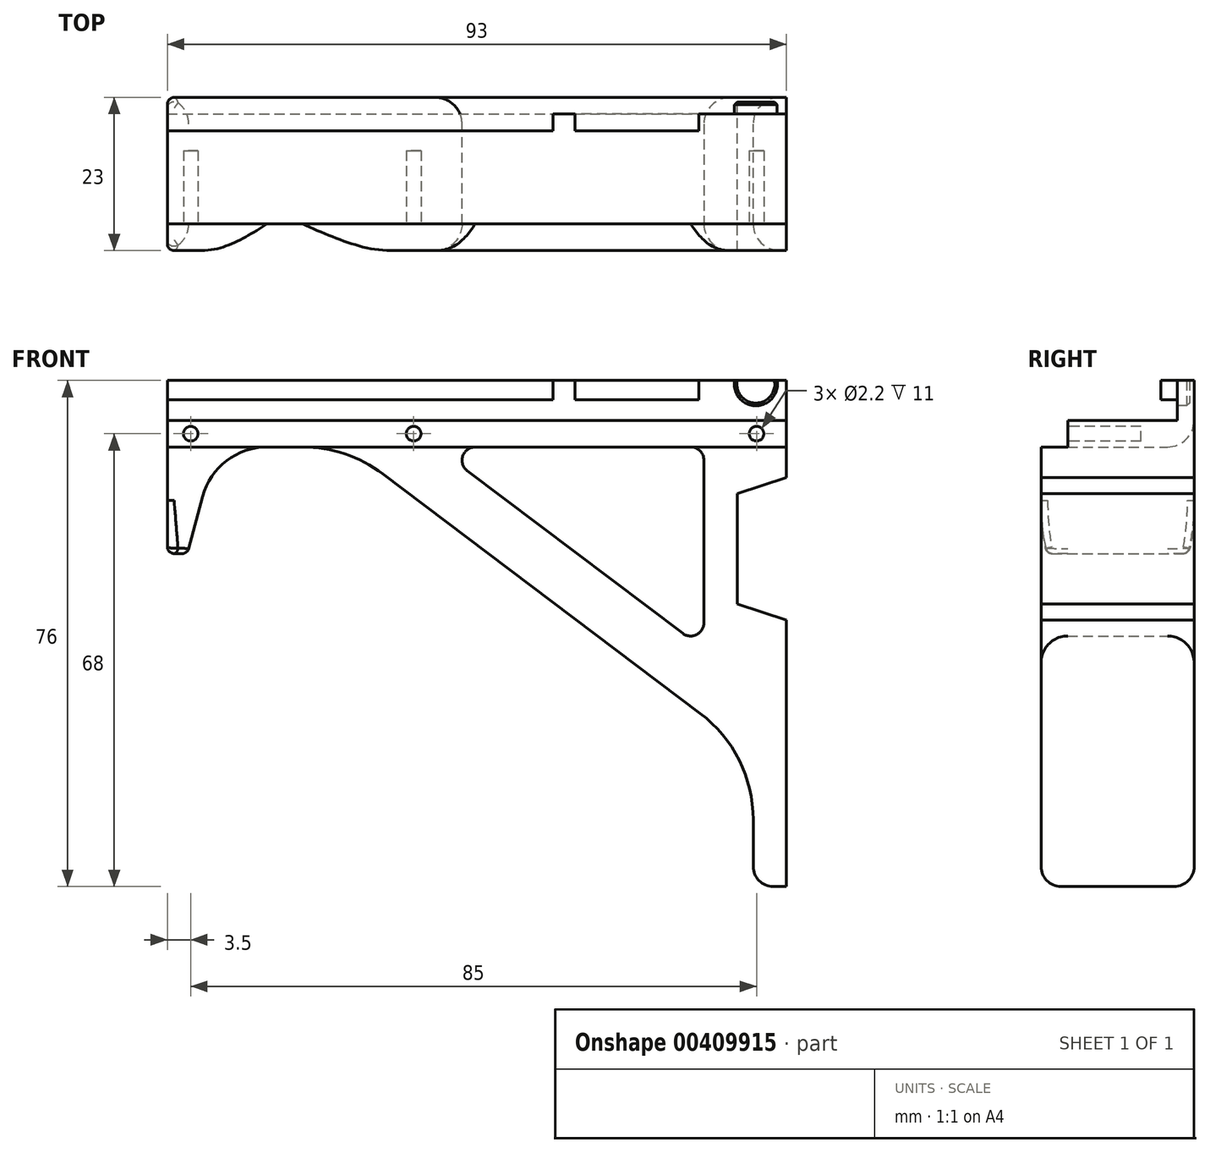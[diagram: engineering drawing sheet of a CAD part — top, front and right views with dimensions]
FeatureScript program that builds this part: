
annotation { "Feature Type Name" : "Feature", "Feature Type Description" : "" }
export const myFeature = defineFeature(function(context is Context, id is Id, definition is map)
    precondition{}
    {
        {
            var Q0;
            Q0=qCreatedBy(makeId("Front.planeOp"),FACE);
            var sketch = newSketch(context, id + "F0", { "sketchPlane" : qUnion([Q0])});
            skLineSegment(sketch, "E0", {"start": v(0, 0) * mm, "end": v(-93, 0) * mm});
            skLineSegment(sketch, "E1", {"start": v(0, 0) * mm, "end": v(0, -8.6) * mm});
            skLineSegment(sketch, "E2.0", {"start": v(0, -8.6) * mm, "end": v(-93, -8.6) * mm, "construction": true});
            skLineSegment(sketch, "E3.0", {"start": v(-7.4, 0) * mm, "end": v(-7.4, -30) * mm, "construction": true});
            skLineSegment(sketch, "E4.0", {"start": v(0, -30) * mm, "end": v(-93, -30) * mm, "construction": true});
            skLineSegment(sketch, "E5.0", {"start": v(0, -11) * mm, "end": v(-93, -11) * mm, "construction": true});
            skLineSegment(sketch, "E6.0", {"start": v(0, -27.6) * mm, "end": v(-93, -27.6) * mm, "construction": true});
            skLineSegment(sketch, "E7", {"start": v(0, -8.6) * mm, "end": v(-7.4, -11) * mm});
            skLineSegment(sketch, "E8", {"start": v(-7.4, -11) * mm, "end": v(-7.4, -27.6) * mm});
            skLineSegment(sketch, "E9", {"start": v(-7.4, -27.6) * mm, "end": v(0, -30) * mm});
            skLineSegment(sketch, "E10.trimOffspring", {"start": v(0, -30) * mm, "end": v(0, -70) * mm});
            skLineSegment(sketch, "E11.0", {"start": v(-5, -59.97) * mm, "end": v(-5, -70) * mm});
            skLineSegment(sketch, "E12", {"start": v(0, -70) * mm, "end": v(-5, -70) * mm});
            skLineSegment(sketch, "E13.0", {"start": v(-72.7, -4) * mm, "end": v(-78.04, -4) * mm});
            skLineSegment(sketch, "E14.0", {"start": v(-90, -20) * mm, "end": v(-93, -20) * mm});
            skLineSegment(sketch, "E15", {"start": v(-93, 0) * mm, "end": v(-93, -20) * mm});
            skLineSegment(sketch, "E16.0", {"start": v(-90, -11) * mm, "end": v(-90, -20) * mm, "construction": true});
            skLineSegment(sketch, "E17", {"start": v(-90, -20) * mm, "end": v(-87.7, -11.41) * mm});
            skLineSegment(sketch, "E18.0", {"start": v(-66, -5) * mm, "end": v(-66, -20) * mm, "construction": true});
            skLineSegment(sketch, "E19.0", {"start": v(0, -50) * mm, "end": v(-5, -50) * mm, "construction": true});
            skLineSegment(sketch, "E20", {"start": v(-60.65, -8.03) * mm, "end": v(-12.96, -44) * mm});
            skPoint(sketch, "E21.visualSharp", {"position": v(-85.71, -4) * mm});
            skArc(sketch, "E21.filletArc", {"start": v(-78.04, -4) * mm, "mid": v(-84.13, -6.07) * mm, "end": v(-87.7, -11.41) * mm});
            skPoint(sketch, "E22.visualSharp", {"position": v(-66, -4) * mm});
            skArc(sketch, "E22.filletArc", {"start": v(-60.65, -8.03) * mm, "mid": v(-66.35, -5.03) * mm, "end": v(-72.7, -4) * mm});
            skPoint(sketch, "E23.visualSharp", {"position": v(-5, -50) * mm});
            skArc(sketch, "E23.filletArc", {"start": v(-5, -59.97) * mm, "mid": v(-7.1, -51.05) * mm, "end": v(-12.96, -44) * mm});
            skSolve(sketch);
        }
        {
            var Q0;
            Q0 = qSketchRegion(id + "F0", true);
            extrude(context, id + "F1", {"entities" : qUnion([Q0]), "depth" : 23 * mm});
        }
        {
            var Q0;
            Q0=makeQuery(id+"F1.opExtrude","SWEPT_FACE",FACE,{"disambiguationData":[OSD([sQuery(id+"F0.wireOp",EDGE,"E20")])]});
            var Q1;
            Q1=makeQuery(id+"F1.opExtrude","SWEPT_FACE",FACE,{"disambiguationData":[OSD([sQuery(id+"F0.wireOp",EDGE,"E13.0")])]});
            fillet(context, id + "F2", {"entities" : qUnion([Q0, Q1]), "radius" : 4 * mm, "tangentPropagation" : true, "allowEdgeOverflow" : false});
        }
        {
            var Q0;
            Q0=makeQuery(id+"F1.opExtrude","SWEPT_FACE",FACE,{"disambiguationData":[OSD([sQuery(id+"F0.wireOp",EDGE,"E0")])]});
            var sketch = newSketch(context, id + "F3", { "sketchPlane" : qUnion([Q0])});
            skLineSegment(sketch, "E24", {"start": v(-93, 0) * mm, "end": v(0, 0) * mm});
            skLineSegment(sketch, "E25.0", {"start": v(-93, -2.5) * mm, "end": v(0, -2.5) * mm});
            skLineSegment(sketch, "E26", {"start": v(-93, 0) * mm, "end": v(-93, -2.5) * mm});
            skLineSegment(sketch, "E27", {"start": v(0, 0) * mm, "end": v(0, -2.5) * mm});
            skLineSegment(sketch, "E28", {"start": v(-93, -23) * mm, "end": v(0, -23) * mm});
            skLineSegment(sketch, "E29", {"start": v(0, -23) * mm, "end": v(0, -20.5) * mm});
            skLineSegment(sketch, "E30", {"start": v(0, -20.5) * mm, "end": v(-93, -20.5) * mm});
            skLineSegment(sketch, "E31", {"start": v(-93, -20.5) * mm, "end": v(-93, -23) * mm});
            skSolve(sketch);
        }
        {
            var Q0;
            Q0 = qSketchRegion(id + "F3", true);
            extrude(context, id + "F4", {"entities" : qUnion([Q0]), "operationType" : NewBodyOperationType.ADD, "depth" : 6 * mm});
        }
        {
            var Q0;
            Q0=makeQuery(id+"F4.opExtrude","SWEPT_FACE",FACE,{"disambiguationData":[OSD([sQuery(id+"F3.wireOp",EDGE,"E25.0")])]});
            var sketch = newSketch(context, id + "F5", { "sketchPlane" : qUnion([Q0])});
            skLineSegment(sketch, "E32", {"start": v(-93, 6) * mm, "end": v(-35.1, 6) * mm});
            skLineSegment(sketch, "E33", {"start": v(0, 6) * mm, "end": v(0, 3.1) * mm, "construction": true});
            skLineSegment(sketch, "E34", {"start": v(-13.2, 3.1) * mm, "end": v(-31.8, 3.1) * mm});
            skLineSegment(sketch, "E35", {"start": v(-93, 3.1) * mm, "end": v(-93, 6) * mm});
            skLineSegment(sketch, "E36.0", {"start": v(-13.2, 6) * mm, "end": v(-13.2, 3.1) * mm});
            skLineSegment(sketch, "E37.0", {"start": v(-31.8, 6) * mm, "end": v(-31.8, 3.1) * mm});
            skLineSegment(sketch, "E38.0", {"start": v(-35.1, 6) * mm, "end": v(-35.1, 3.1) * mm});
            skLineSegment(sketch, "E39.trimOffspring", {"start": v(-31.8, 6) * mm, "end": v(-13.2, 6) * mm});
            skLineSegment(sketch, "E40.trimOffspring", {"start": v(-35.1, 3.1) * mm, "end": v(-93, 3.1) * mm});
            skSolve(sketch);
        }
        {
            var Q0;
            Q0 = qSketchRegion(id + "F5", true);
            extrude(context, id + "F6", {"entities" : qUnion([Q0]), "operationType" : NewBodyOperationType.ADD, "depth" : 2.5 * mm});
        }
        {
            var Q0;
            Q0=makeQuery(id+"F4.opExtrude","SWEPT_FACE",FACE,{"disambiguationData":[OSD([sQuery(id+"F3.wireOp",EDGE,"E30")])]});
            var sketch = newSketch(context, id + "F7", { "sketchPlane" : qUnion([Q0])});
            skLineSegment(sketch, "E41", {"start": v(13.2, 6) * mm, "end": v(31.8, 6) * mm});
            skLineSegment(sketch, "E42", {"start": v(93, 6) * mm, "end": v(93, 3.1) * mm});
            skLineSegment(sketch, "E43", {"start": v(93, 3.1) * mm, "end": v(35.1, 3.1) * mm});
            skLineSegment(sketch, "E44", {"start": v(0, 3.1) * mm, "end": v(0, 6) * mm, "construction": true});
            skLineSegment(sketch, "E45.0", {"start": v(13.2, 3.1) * mm, "end": v(13.2, 6) * mm});
            skLineSegment(sketch, "E46.0", {"start": v(31.8, 3.1) * mm, "end": v(31.8, 6) * mm});
            skLineSegment(sketch, "E47.0", {"start": v(35.1, 3.1) * mm, "end": v(35.1, 6) * mm});
            skLineSegment(sketch, "E48.trimOffspring", {"start": v(35.1, 6) * mm, "end": v(93, 6) * mm});
            skLineSegment(sketch, "E49.trimOffspring", {"start": v(31.8, 3.1) * mm, "end": v(13.2, 3.1) * mm});
            skSolve(sketch);
        }
        {
            var Q0;
            Q0 = qSketchRegion(id + "F7", true);
            extrude(context, id + "F8", {"entities" : qUnion([Q0]), "operationType" : NewBodyOperationType.ADD, "depth" : 2.5 * mm});
        }
        {
            var Q0;
            {var subQ0=makeQuery(id+"F1.opExtrude","CAP_FACE",FACE,{"disambiguationData":[OSD([sQuery(id+"F0.wireOp",EDGE,"E0"),sQuery(id+"F0.wireOp",EDGE,"E1"),sQuery(id+"F0.wireOp",EDGE,"E7"),sQuery(id+"F0.wireOp",EDGE,"E8"),sQuery(id+"F0.wireOp",EDGE,"E9"),sQuery(id+"F0.wireOp",EDGE,"E10.trimOffspring"),sQuery(id+"F0.wireOp",EDGE,"E11.0"),sQuery(id+"F0.wireOp",EDGE,"E12"),sQuery(id+"F0.wireOp",EDGE,"E13.0"),sQuery(id+"F0.wireOp",EDGE,"E14.0"),sQuery(id+"F0.wireOp",EDGE,"E15"),sQuery(id+"F0.wireOp",EDGE,"E17"),sQuery(id+"F0.wireOp",EDGE,"E20")])],"isStart":false});Q0=makeQuery(id+"F4.boolean.opBoolean","MERGE",FACE,{"derivedFrom":[makeQuery(id+"F2.opFillet","SPLIT",FACE,{"disambiguationData":[OD(0.0)],"derivedFrom":subQ0}),makeQuery(id+"F2.opFillet","SPLIT",FACE,{"disambiguationData":[OD(1.0)],"derivedFrom":subQ0}),makeQuery(id+"F4.opExtrude","SWEPT_FACE",FACE,{"disambiguationData":[OSD([sQuery(id+"F3.wireOp",EDGE,"E28")])]})]});}
            var sketch = newSketch(context, id + "F9", { "sketchPlane" : qUnion([Q0])});
            skLineSegment(sketch, "E50", {"start": v(-52.71, -4) * mm, "end": v(-12.4, -4) * mm});
            skLineSegment(sketch, "E51", {"start": v(-12.4, -4) * mm, "end": v(-12.4, -34.4) * mm});
            skLineSegment(sketch, "E52", {"start": v(-12.4, -34.4) * mm, "end": v(-52.71, -4) * mm});
            skSolve(sketch);
        }
        {
            var Q0;
            Q0 = qSketchRegion(id + "F9", true);
            extrude(context, id + "F10", {"entities" : qUnion([Q0]), "operationType" : NewBodyOperationType.REMOVE, "endBound" : BoundingType.THROUGH_ALL, "oppositeDirection" : true, "depth" : 25 * mm});
        }
        {
            var Q0;
            Q0=makeQuery(id+"F10.boolean.opBoolean","COPY",EDGE,{"derivedFrom":makeQuery(id+"F10.opExtrude","SWEPT_EDGE",EDGE,{"disambiguationData":[OSD([sQuery(id+"F9.wireOp",EDGE,"E50"),sQuery(id+"F9.wireOp",EDGE,"E52")])]})});
            var Q1;
            Q1=makeQuery(id+"F10.boolean.opBoolean","COPY",EDGE,{"derivedFrom":makeQuery(id+"F10.opExtrude","SWEPT_EDGE",EDGE,{"disambiguationData":[OSD([sQuery(id+"F9.wireOp",EDGE,"E50"),sQuery(id+"F9.wireOp",EDGE,"E51")])]})});
            var Q2;
            Q2=makeQuery(id+"F10.boolean.opBoolean","COPY",EDGE,{"derivedFrom":makeQuery(id+"F10.opExtrude","SWEPT_EDGE",EDGE,{"disambiguationData":[OSD([sQuery(id+"F9.wireOp",EDGE,"E51"),sQuery(id+"F9.wireOp",EDGE,"E52")])]})});
            fillet(context, id + "F11", {"entities" : qUnion([Q0, Q1, Q2]), "radius" : 2 * mm, "tangentPropagation" : true, "allowEdgeOverflow" : false});
        }
        {
            var Q0;
            Q0=makeQuery(id+"F10.boolean.opBoolean","COPY",FACE,{"derivedFrom":makeQuery(id+"F10.opExtrude","SWEPT_FACE",FACE,{"disambiguationData":[OSD([sQuery(id+"F9.wireOp",EDGE,"E52")])]})});
            var Q1;
            Q1=makeQuery(id+"F11.opFillet","BLEND_FACE",FACE,{"disambiguationData":[OSD([sQuery(id+"F9.wireOp",EDGE,"E50"),sQuery(id+"F9.wireOp",EDGE,"E52")])]});
            var Q2;
            Q2=makeQuery(id+"F11.opFillet","BLEND_FACE",FACE,{"disambiguationData":[OSD([sQuery(id+"F9.wireOp",EDGE,"E51"),sQuery(id+"F9.wireOp",EDGE,"E52")])]});
            var Q3;
            Q3=makeQuery(id+"F10.boolean.opBoolean","COPY",FACE,{"derivedFrom":makeQuery(id+"F10.opExtrude","SWEPT_FACE",FACE,{"disambiguationData":[OSD([sQuery(id+"F9.wireOp",EDGE,"E51")])]})});
            var Q4;
            Q4=makeQuery(id+"F11.opFillet","BLEND_FACE",FACE,{"disambiguationData":[OSD([sQuery(id+"F9.wireOp",EDGE,"E50"),sQuery(id+"F9.wireOp",EDGE,"E51")])]});
            var Q5;
            Q5=makeQuery(id+"F10.boolean.opBoolean","COPY",FACE,{"derivedFrom":makeQuery(id+"F10.opExtrude","SWEPT_FACE",FACE,{"disambiguationData":[OSD([sQuery(id+"F9.wireOp",EDGE,"E50")])]})});
            fillet(context, id + "F12", {"entities" : qUnion([Q0, Q1, Q2, Q3, Q4, Q5]), "radius" : 4 * mm, "tangentPropagation" : true, "allowEdgeOverflow" : false});
        }
        {
            var Q0;
            Q0=makeQuery(id+"F1.opExtrude","SWEPT_FACE",FACE,{"disambiguationData":[OSD([sQuery(id+"F0.wireOp",EDGE,"E14.0")])]});
            var Q1;
            Q1=makeQuery(id+"F4.boolean.opBoolean","MERGE",EDGE,{"derivedFrom":[makeQuery(id+"F1.opExtrude","CAP_EDGE",EDGE,{"disambiguationData":[OSD([sQuery(id+"F0.wireOp",EDGE,"E15")])],"isStart":false}),makeQuery(id+"F4.opExtrude","SWEPT_EDGE",EDGE,{"disambiguationData":[OSD([sQuery(id+"F3.wireOp",EDGE,"E28"),sQuery(id+"F3.wireOp",EDGE,"E31")])]})]});
            var Q2;
            Q2=makeQuery(id+"F4.boolean.opBoolean","MERGE",EDGE,{"derivedFrom":[makeQuery(id+"F1.opExtrude","CAP_EDGE",EDGE,{"disambiguationData":[OSD([sQuery(id+"F0.wireOp",EDGE,"E15")])],"isStart":true}),makeQuery(id+"F4.opExtrude","SWEPT_EDGE",EDGE,{"disambiguationData":[OSD([sQuery(id+"F3.wireOp",EDGE,"E24"),sQuery(id+"F3.wireOp",EDGE,"E26")])]})]});
            fillet(context, id + "F13", {"entities" : qUnion([Q0, Q1, Q2]), "radius" : 1 * mm, "tangentPropagation" : true, "allowEdgeOverflow" : false});
        }
        {
            var Q0;
            Q0=makeQuery(id+"F4.opExtrude","SWEPT_FACE",FACE,{"disambiguationData":[OSD([sQuery(id+"F3.wireOp",EDGE,"E25.0")])]});
            var sketch = newSketch(context, id + "F14", { "sketchPlane" : qUnion([Q0])});
            skCircle(sketch, "E53", {"center": v(-4.6, 5.45) * mm, "radius": 3.25 * mm});
            skSolve(sketch);
        }
        {
            var Q0;
            Q0 = qSketchRegion(id + "F14", true);
            extrude(context, id + "F15", {"entities" : qUnion([Q0]), "operationType" : NewBodyOperationType.REMOVE, "oppositeDirection" : true, "depth" : 1.8 * mm});
        }
        {
            var Q0;
            Q0=makeQuery(id+"F15.boolean.opBoolean","COPY",EDGE,{"derivedFrom":makeQuery(id+"F15.opExtrude","CAP_EDGE",EDGE,{"disambiguationData":[OSD([sQuery(id+"F14.wireOp",EDGE,"E53")])],"isStart":false})});
            chamfer(context, id + "F16", {"entities" : qUnion([Q0]), "width" : .4 * mm, "tangentPropagation" : true});
        }
        {
            var Q0;
            Q0=makeQuery(id+"F4.opExtrude","SWEPT_FACE",FACE,{"disambiguationData":[OSD([sQuery(id+"F3.wireOp",EDGE,"E30")])]});
            var sketch = newSketch(context, id + "F17", { "sketchPlane" : qUnion([Q0])});
            skCircle(sketch, "E54", {"center": v(4.6, 5.45) * mm, "radius": 3.25 * mm});
            skSolve(sketch);
        }
        {
            var Q0;
            Q0 = qSketchRegion(id + "F17", true);
            extrude(context, id + "F18", {"entities" : qUnion([Q0]), "operationType" : NewBodyOperationType.REMOVE, "oppositeDirection" : true, "depth" : 1.8 * mm});
        }
        {
            var Q0;
            Q0=makeQuery(id+"F18.boolean.opBoolean","COPY",EDGE,{"derivedFrom":makeQuery(id+"F18.opExtrude","CAP_EDGE",EDGE,{"disambiguationData":[OSD([sQuery(id+"F17.wireOp",EDGE,"E54")])],"isStart":false})});
            chamfer(context, id + "F19", {"entities" : qUnion([Q0]), "width" : .4 * mm, "tangentPropagation" : true});
        }
        {
            var Q0;
            {var subQ0=makeQuery(id+"F1.opExtrude","CAP_FACE",FACE,{"disambiguationData":[OSD([sQuery(id+"F0.wireOp",EDGE,"E0"),sQuery(id+"F0.wireOp",EDGE,"E1"),sQuery(id+"F0.wireOp",EDGE,"E7"),sQuery(id+"F0.wireOp",EDGE,"E8"),sQuery(id+"F0.wireOp",EDGE,"E9"),sQuery(id+"F0.wireOp",EDGE,"E10.trimOffspring"),sQuery(id+"F0.wireOp",EDGE,"E11.0"),sQuery(id+"F0.wireOp",EDGE,"E12"),sQuery(id+"F0.wireOp",EDGE,"E13.0"),sQuery(id+"F0.wireOp",EDGE,"E14.0"),sQuery(id+"F0.wireOp",EDGE,"E15"),sQuery(id+"F0.wireOp",EDGE,"E17"),sQuery(id+"F0.wireOp",EDGE,"E20")])],"isStart":false});Q0=makeQuery(id+"F4.boolean.opBoolean","MERGE",FACE,{"derivedFrom":[makeQuery(id+"F2.opFillet","SPLIT",FACE,{"disambiguationData":[OD(0.0)],"derivedFrom":subQ0}),makeQuery(id+"F2.opFillet","SPLIT",FACE,{"disambiguationData":[OD(1.0)],"derivedFrom":subQ0}),makeQuery(id+"F4.opExtrude","SWEPT_FACE",FACE,{"disambiguationData":[OSD([sQuery(id+"F3.wireOp",EDGE,"E28")])]})]});}
            var sketch = newSketch(context, id + "F20", { "sketchPlane" : qUnion([Q0])});
            skCircle(sketch, "E55", {"center": v(-4.5, -2) * mm, "radius": 1.1 * mm});
            skCircle(sketch, "E56", {"center": v(-56, -2) * mm, "radius": 1.1 * mm});
            skCircle(sketch, "E57", {"center": v(-89.5, -2) * mm, "radius": 1.1 * mm});
            skSolve(sketch);
        }
        {
            var Q0;
            Q0 = qSketchRegion(id + "F20", true);
            extrude(context, id + "F21", {"entities" : qUnion([Q0]), "operationType" : NewBodyOperationType.REMOVE, "oppositeDirection" : true, "depth" : 15 * mm});
        }
        {
            var Q0;
            Q0=makeQuery(id+"F4.boolean.opBoolean","MERGE",FACE,{"derivedFrom":[makeQuery(id+"F1.opExtrude","SWEPT_FACE",FACE,{"disambiguationData":[OSD([sQuery(id+"F0.wireOp",EDGE,"E1")])]}),makeQuery(id+"F4.opExtrude","SWEPT_FACE",FACE,{"disambiguationData":[OSD([sQuery(id+"F3.wireOp",EDGE,"E27")])]}),makeQuery(id+"F4.opExtrude","SWEPT_FACE",FACE,{"disambiguationData":[OSD([sQuery(id+"F3.wireOp",EDGE,"E29")])]})]});
            var sketch = newSketch(context, id + "F22", { "sketchPlane" : qUnion([Q0])});
            skLineSegment(sketch, "E58.bottom", {"start": v(-23, 6) * mm, "end": v(-19, 6) * mm});
            skLineSegment(sketch, "E58.top", {"start": v(-23, -4) * mm, "end": v(-19, -4) * mm});
            skLineSegment(sketch, "E58.left", {"start": v(-23, 6) * mm, "end": v(-23, -4) * mm});
            skLineSegment(sketch, "E58.right", {"start": v(-19, 3.1) * mm, "end": v(-19, -4) * mm});
            skLineSegment(sketch, "E59.bottom", {"start": v(-19, 6) * mm, "end": v(-18, 6) * mm});
            skLineSegment(sketch, "E59.top", {"start": v(-19, 3.1) * mm, "end": v(-18, 3.1) * mm});
            skLineSegment(sketch, "E59.right", {"start": v(-18, 6) * mm, "end": v(-18, 3.1) * mm});
            skSolve(sketch);
        }
        {
            var Q0;
            Q0 = qSketchRegion(id + "F22", true);
            extrude(context, id + "F23", {"entities" : qUnion([Q0]), "operationType" : NewBodyOperationType.REMOVE, "endBound" : BoundingType.THROUGH_ALL, "oppositeDirection" : true, "depth" : 25 * mm});
        }
        {
            var Q0;
            Q0=makeQuery(id+"F2.opFillet","BLEND_EDGE",EDGE,{"blendedFrom":[makeQuery(id+"F1.opExtrude","CAP_EDGE",EDGE,{"disambiguationData":[OSD([sQuery(id+"F0.wireOp",EDGE,"E11.0")])],"isStart":false}),makeQuery(id+"F1.opExtrude","SWEPT_FACE",FACE,{"disambiguationData":[OSD([sQuery(id+"F0.wireOp",EDGE,"E12")])]})],"blendedInto":[makeQuery(id+"F1.opExtrude","SWEPT_FACE",FACE,{"disambiguationData":[OSD([sQuery(id+"F0.wireOp",EDGE,"E12")])]})]});
            var Q1;
            Q1=makeQuery(id+"F1.opExtrude","SWEPT_EDGE",EDGE,{"disambiguationData":[OSD([sQuery(id+"F0.wireOp",EDGE,"E11.0"),sQuery(id+"F0.wireOp",EDGE,"E12")])]});
            var Q2;
            Q2=makeQuery(id+"F2.opFillet","BLEND_EDGE",EDGE,{"blendedFrom":[makeQuery(id+"F1.opExtrude","CAP_EDGE",EDGE,{"disambiguationData":[OSD([sQuery(id+"F0.wireOp",EDGE,"E11.0")])],"isStart":true}),makeQuery(id+"F1.opExtrude","SWEPT_FACE",FACE,{"disambiguationData":[OSD([sQuery(id+"F0.wireOp",EDGE,"E12")])]})],"blendedInto":[makeQuery(id+"F1.opExtrude","SWEPT_FACE",FACE,{"disambiguationData":[OSD([sQuery(id+"F0.wireOp",EDGE,"E12")])]})]});
            fillet(context, id + "F24", {"entities" : qUnion([Q0, Q1, Q2]), "radius" : 3 * mm, "tangentPropagation" : true, "allowEdgeOverflow" : false});
        }
    });
